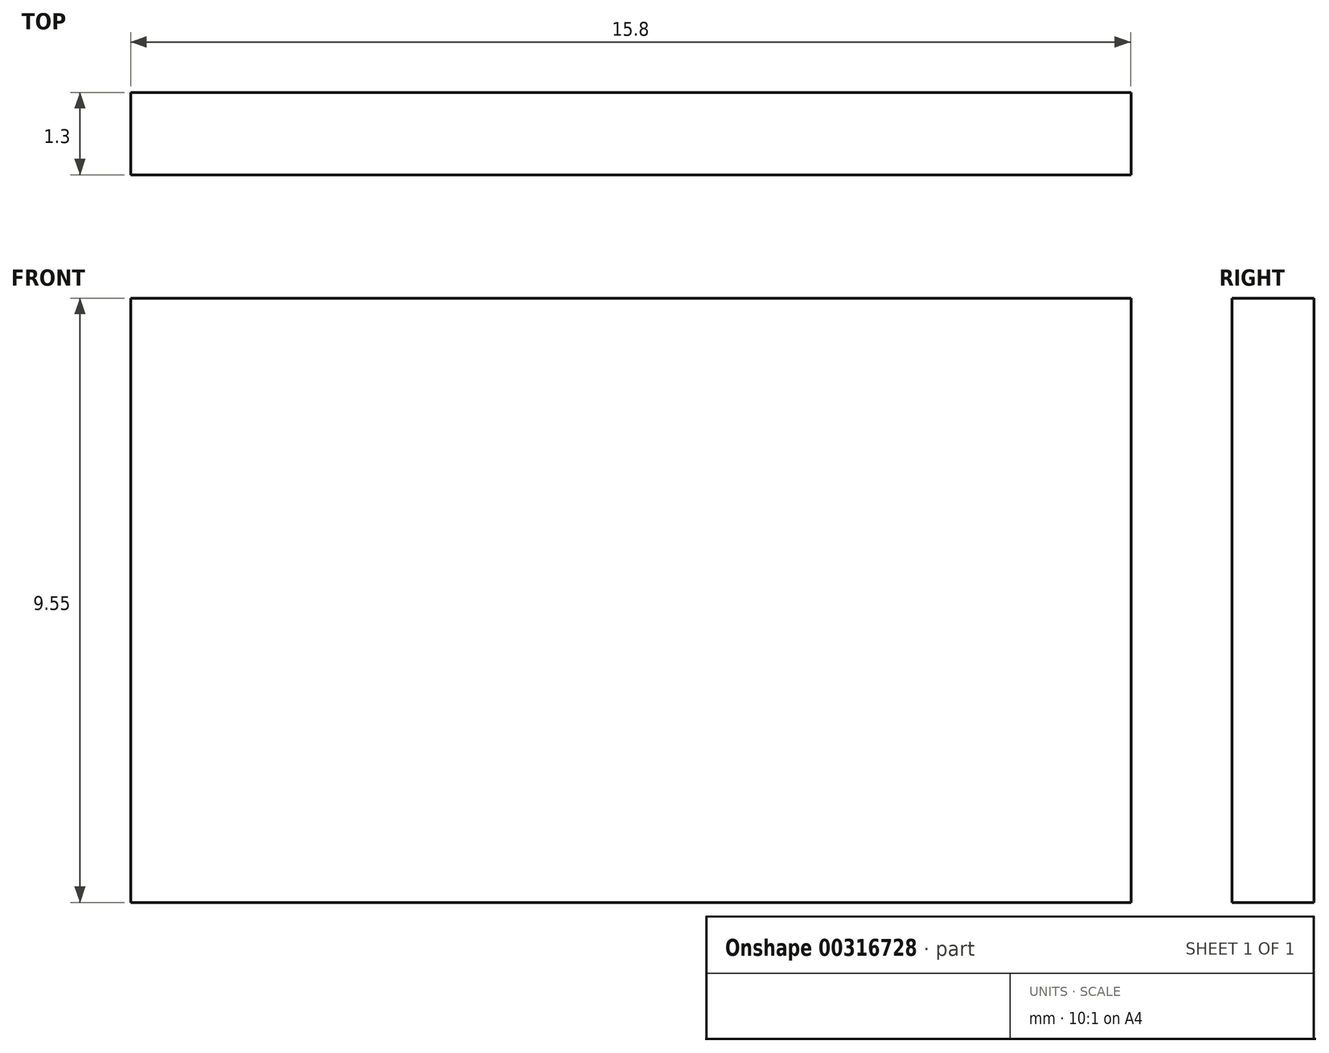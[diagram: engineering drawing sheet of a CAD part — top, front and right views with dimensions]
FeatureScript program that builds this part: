
annotation { "Feature Type Name" : "Feature", "Feature Type Description" : "" }
export const myFeature = defineFeature(function(context is Context, id is Id, definition is map)
    precondition{}
    {
        {
            var Q0;
            Q0=qCreatedBy(makeId("Front.planeOp"),FACE);
            var sketch = newSketch(context, id + "F0", { "sketchPlane" : qUnion([Q0])});
            skLineSegment(sketch, "E0.bottom", {"start": v(-37.53, 9.55) * mm, "end": v(-21.73, 9.55) * mm});
            skLineSegment(sketch, "E0.top", {"start": v(-37.53, 0) * mm, "end": v(-21.73, 0) * mm});
            skLineSegment(sketch, "E0.left", {"start": v(-37.53, 9.55) * mm, "end": v(-37.53, 0) * mm});
            skLineSegment(sketch, "E0.right", {"start": v(-21.73, 9.55) * mm, "end": v(-21.73, 0) * mm});
            skSolve(sketch);
        }
        {
            var Q0;
            Q0=makeQuery(id+"F0.imprint","IMPRINT",FACE,{"disambiguationData":[TD([[makeQuery(id+"F0.imprint","IMPRINT",EDGE,{"derivedFrom":sQuery(id+"F0.wireOp",EDGE,"E0.bottom")}),-1.0]])]});
            extrude(context, id + "F1", {"entities" : qUnion([Q0]), "depth" : 1.3 * mm});
        }
    });
